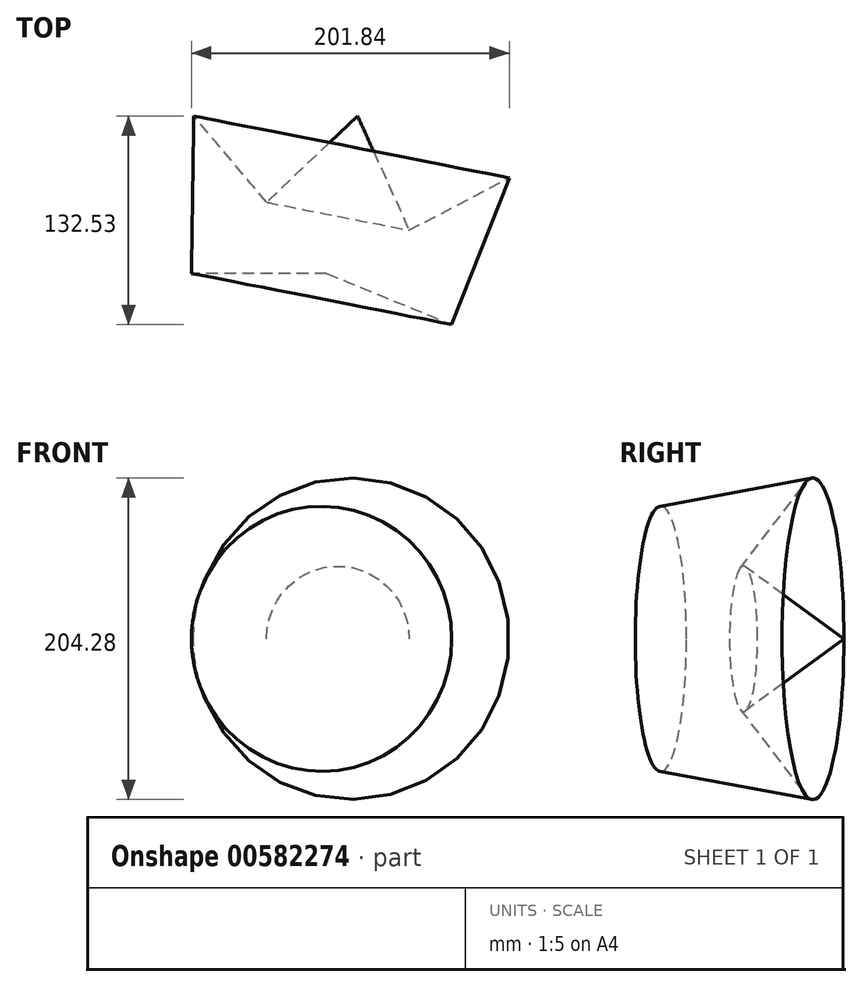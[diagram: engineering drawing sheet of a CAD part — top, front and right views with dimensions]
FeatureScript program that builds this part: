
annotation { "Feature Type Name" : "Feature", "Feature Type Description" : "" }
export const myFeature = defineFeature(function(context is Context, id is Id, definition is map)
    precondition{}
    {
        {
            var Q0;
            Q0=qCreatedBy(makeId("Top.planeOp"),FACE);
            var sketch = newSketch(context, id + "F0", { "sketchPlane" : qUnion([Q0])});
            skLineSegment(sketch, "E0", {"start": v(-46.5, 55.07) * mm, "end": v(37.95, -45) * mm});
            skLineSegment(sketch, "E1", {"start": v(37.95, -45) * mm, "end": v(-47.87, -45) * mm});
            skLineSegment(sketch, "E2", {"start": v(-47.87, -45) * mm, "end": v(57.6, 55.07) * mm});
            skLineSegment(sketch, "E3", {"start": v(57.6, 55.07) * mm, "end": v(-46.5, 55.07) * mm});
            skLineSegment(sketch, "E4", {"start": v(57.6, 55.07) * mm, "end": v(37.95, -45) * mm});
            skLineSegment(sketch, "E5", {"start": v(-46.5, 55.07) * mm, "end": v(-47.87, -45) * mm});
            skSolve(sketch);
        }
        {
            var Q0;
            {var subQ0=sQuery(id+"F0.wireOp",EDGE,"E5");Q0=makeQuery(id+"F0.imprint","IMPRINT",FACE,{"disambiguationData":[TD([[makeQuery(id+"F0.imprint","IMPRINT",EDGE,{"derivedFrom":subQ0}),1.0]])]});}
            var Q1;
            {var subQ0=sQuery(id+"F0.wireOp",EDGE,"E1");Q1=makeQuery(id+"F0.imprint","IMPRINT",FACE,{"disambiguationData":[TD([[makeQuery(id+"F0.imprint","IMPRINT",EDGE,{"derivedFrom":subQ0}),-1.0]])]});}
            var Q2;
            {var subQ0=sQuery(id+"F0.wireOp",EDGE,"E4");Q2=makeQuery(id+"F0.imprint","IMPRINT",FACE,{"disambiguationData":[TD([[makeQuery(id+"F0.imprint","IMPRINT",EDGE,{"derivedFrom":subQ0}),-1.0]])]});}
            var Q3;
            Q3=sQuery(id+"F0.wireOp",EDGE,"E4");
            revolve(context, id + "F1", {"entities" : qUnion([Q0, Q1, Q2]), "axis" : qUnion([Q3]), "revolveType" : RevolveType.FULL});
        }
    });
